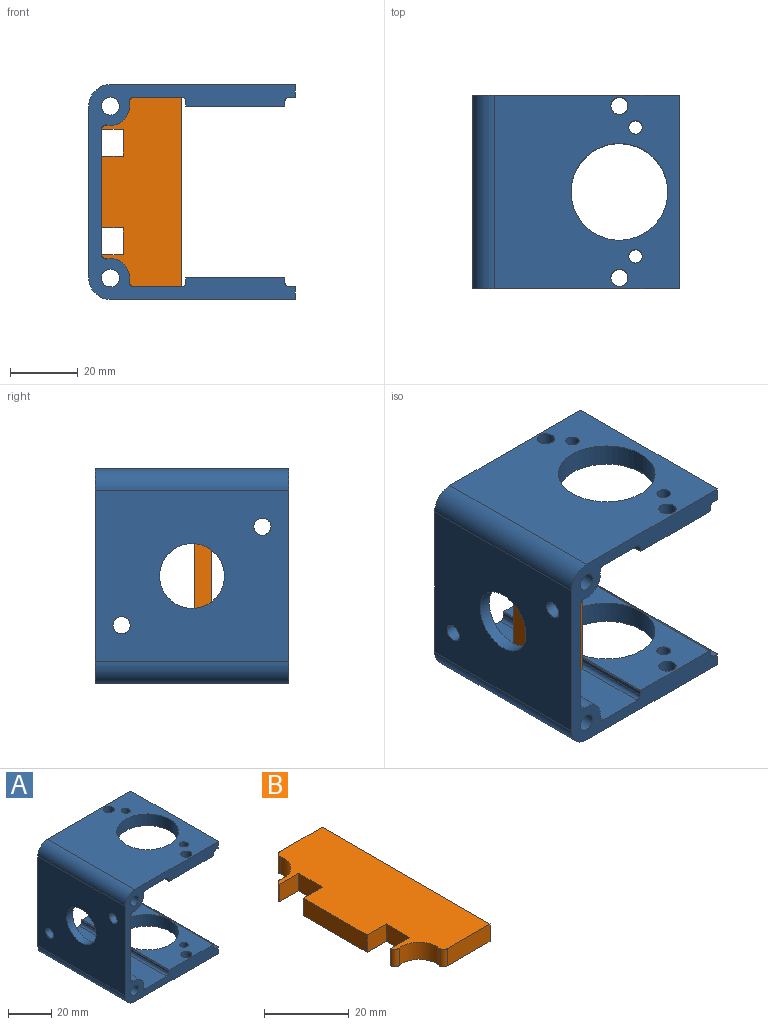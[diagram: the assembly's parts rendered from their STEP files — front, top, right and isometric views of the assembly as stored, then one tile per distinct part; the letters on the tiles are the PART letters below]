
ASSEMBLY  parts=2 mates=1
PART A: 49 faces, bbox 61x57.2x63.5 mm
  f0: plane 57.15x28.7mm, normal (0,0,1), area 933.5mm2, adj f5,f7,f12,f28,f30,f33,f37,f39
  f1: plane 57.15x14.21mm, normal (0,0,1), area 812.3mm2, adj f5,f8,f19,f33
  f2: plane 57.15x37.06mm, normal (1,0,0), area 1789.5mm2, adj f5,f11,f26,f27,f33,f36,f48
  f3: plane 57.15x54.61mm, normal (0,0,-1), area 2414.1mm2, adj f5,f7,f12,f22,f32,f33,f37,f39
  f4: plane 57.15x1.78mm, normal (0,0,1), area 101.6mm2, adj f5,f21,f32,f33
  f5: plane 63.5x60.96mm, normal (0,-1,0), area 902.8mm2, adj f0,f1,f2,f3,f4,f6,f8,f9
  f6: plane 57.15x1.78mm, normal (0,0,-1), area 101.6mm2, adj f5,f31,f33,f44
  f7: cylinder r=2.54mm len=6.6mm, axis (0,0,1), area 105.4mm2, adj f0,f3
  f8: cylinder r=1.27mm len=57.15mm, axis (0,-1,0), area 127.3mm2, adj f1,f5,f14,f33
  f9: cylinder r=2.67mm len=57.15mm, axis (0,-1,0), area 957.7mm2, adj f5,f33
  f10: plane 57.15x50.8mm, normal (-1,0,0), area 2574.6mm2, adj f5,f11,f18,f22,f27,f33,f36
  f11: cylinder r=2.54mm len=5.08mm, axis (1,0,0), area 60.8mm2, adj f2,f10
  f12: cylinder r=14.29mm len=28.58mm, axis (0,0,1), area 592.8mm2, adj f0,f3
  f13: plane 57.15x14.21mm, normal (0,0,-1), area 812.3mm2, adj f5,f17,f20,f33
  f14: cylinder r=5.71mm len=57.15mm, axis (0,-1,0), area 632.5mm2, adj f5,f8,f33,f48
  f15: plane 57.15x1.27mm, normal (-1,0,0), area 72.6mm2, adj f5,f19,f30,f33
  f16: plane 57.15x1.27mm, normal (-1,0,0), area 72.6mm2, adj f5,f20,f33,f46
  f17: cylinder r=1.27mm len=57.15mm, axis (0,-1,0), area 127.3mm2, adj f5,f13,f24,f33
  f18: cylinder r=6.35mm len=57.15mm, axis (0,1,0), area 570mm2, adj f5,f10,f25,f33
  f19: cylinder r=1.27mm len=57.15mm, axis (0,1,0), area 114mm2, adj f1,f5,f15,f33
  f20: cylinder r=1.27mm len=57.15mm, axis (0,1,0), area 114mm2, adj f5,f13,f16,f33
  f21: cylinder r=1.27mm len=57.15mm, axis (0,1,0), area 114mm2, adj f4,f5,f33,f45
  f22: cylinder r=6.35mm len=57.15mm, axis (0,1,0), area 570mm2, adj f3,f5,f10,f33
  f23: cylinder r=2.67mm len=57.15mm, axis (0,-1,0), area 957.7mm2, adj f5,f33
  f24: cylinder r=5.71mm len=57.15mm, axis (0,-1,0), area 632.5mm2, adj f5,f17,f26,f33
  f25: plane 57.15x54.61mm, normal (0,0,1), area 2414.1mm2, adj f5,f18,f29,f31,f33,f35,f38,f40
  f26: cylinder r=1.27mm len=57.15mm, axis (0,-1,0), area 127.3mm2, adj f2,f5,f24,f33
  f27: cylinder r=2.54mm len=5.08mm, axis (1,0,0), area 60.8mm2, adj f2,f10
  f28: cylinder r=0.25mm len=57.15mm, axis (0,-1,0), area 22.8mm2, adj f0,f5,f33,f45
  f29: cylinder r=2.54mm len=6.6mm, axis (0,0,1), area 105.4mm2, adj f25,f34
  f30: cylinder r=0.25mm len=57.15mm, axis (0,-1,0), area 22.8mm2, adj f0,f5,f15,f33
  f31: plane 57.15x3.81mm, normal (1,0,0), area 217.7mm2, adj f5,f6,f25,f33
  f32: plane 57.15x3.81mm, normal (1,0,0), area 217.7mm2, adj f3,f4,f5,f33
  f33: plane 63.5x60.96mm, normal (0,1,0), area 902.8mm2, adj f0,f1,f2,f3,f4,f6,f8,f9
  f34: plane 57.15x28.7mm, normal (0,0,-1), area 933.5mm2, adj f5,f29,f33,f35,f38,f40,f42,f46
  f35: cylinder r=14.29mm len=28.58mm, axis (0,0,1), area 592.8mm2, adj f25,f34
  f36: cylinder r=9.58mm len=19.15mm, axis (1,0,0), area 229.2mm2, adj f2,f10
  f37: cylinder r=2.54mm len=6.6mm, axis (0,0,1), area 105.4mm2, adj f0,f3
  f38: cylinder r=2.54mm len=6.6mm, axis (0,0,1), area 105.4mm2, adj f25,f34
  f39: cylinder r=1.99mm len=6.6mm, axis (0,0,1), area 82.7mm2, adj f0,f3
  f40: cylinder r=1.99mm len=6.6mm, axis (0,0,1), area 82.7mm2, adj f25,f34
  f41: cylinder r=1.99mm len=6.6mm, axis (0,0,1), area 82.7mm2, adj f0,f3
  f42: cylinder r=1.99mm len=6.6mm, axis (0,0,1), area 82.7mm2, adj f25,f34
  f43: plane 57.15x1.27mm, normal (1,0,0), area 72.6mm2, adj f5,f33,f44,f47
  f44: cylinder r=1.27mm len=57.15mm, axis (0,1,0), area 114mm2, adj f5,f6,f33,f43
  f45: plane 57.15x1.27mm, normal (1,0,0), area 72.6mm2, adj f5,f21,f28,f33
  f46: cylinder r=0.25mm len=57.15mm, axis (0,-1,0), area 22.8mm2, adj f5,f16,f33,f34
  f47: cylinder r=0.25mm len=57.15mm, axis (0,-1,0), area 22.8mm2, adj f5,f33,f34,f43
  f48: cylinder r=1.27mm len=57.15mm, axis (0,-1,0), area 127.3mm2, adj f2,f5,f14,f33
PART B: 18 faces, bbox 23.6x55.9x5 mm
  f0: cylinder r=5.71mm len=6.75mm, axis (0,0,-1), area 55.3mm2, adj f1,f15,f16,f17
  f1: cylinder r=1.27mm len=5mm, axis (0,0,-1), area 11.1mm2, adj f0,f2,f16,f17
  f2: plane 6.35x5mm, normal (0,-1,0), area 31.8mm2, adj f1,f3,f16,f17
  f3: plane 7.93x5mm, normal (-1,0,0), area 39.6mm2, adj f2,f4,f16,f17
  f4: plane 6.35x5mm, normal (0,1,0), area 31.8mm2, adj f3,f5,f16,f17
  f5: plane 21.21x5mm, normal (-1,0,0), area 106.1mm2, adj f4,f6,f16,f17
  f6: plane 6.35x5mm, normal (0,-1,0), area 31.8mm2, adj f5,f7,f16,f17
  f7: plane 7.93x5mm, normal (-1,0,0), area 39.6mm2, adj f6,f8,f16,f17
  f8: plane 6.35x5mm, normal (0,1,0), area 31.8mm2, adj f7,f9,f16,f17
  f9: cylinder r=1.27mm len=5mm, axis (0,0,-1), area 11.1mm2, adj f8,f10,f16,f17
  f10: cylinder r=5.71mm len=6.75mm, axis (0,0,-1), area 55.3mm2, adj f9,f11,f16,f17
  f11: cylinder r=1.27mm len=5mm, axis (0,0,-1), area 11.1mm2, adj f10,f12,f16,f17
  f12: plane 14.21x5mm, normal (0,-1,0), area 71.1mm2, adj f11,f13,f16,f17
  f13: plane 55.88x5mm, normal (1,0,0), area 279.4mm2, adj f12,f14,f16,f17
  f14: plane 14.21x5mm, normal (0,1,0), area 71.1mm2, adj f13,f15,f16,f17
  f15: cylinder r=1.27mm len=5mm, axis (0,0,-1), area 11.1mm2, adj f0,f14,f16,f17
  f16: plane 55.88x23.62mm, normal (0,0,1), area 1096.5mm2, adj f0,f1,f2,f3,f4,f5,f6,f7
  f17: plane 55.88x23.62mm, normal (0,0,-1), area 1096.5mm2, adj f0,f1,f2,f3,f4,f5,f6,f7
PLACE A t=(35.28,-5.51,17.69)mm
PLACE B rot(axis=(1,0,0),90deg) t=(39.09,22.39,-14.06)mm
MATE fastened A.f2 <-> B.f5  axis (1,0,0) through (39.09,-5.51,-14.06)mm
